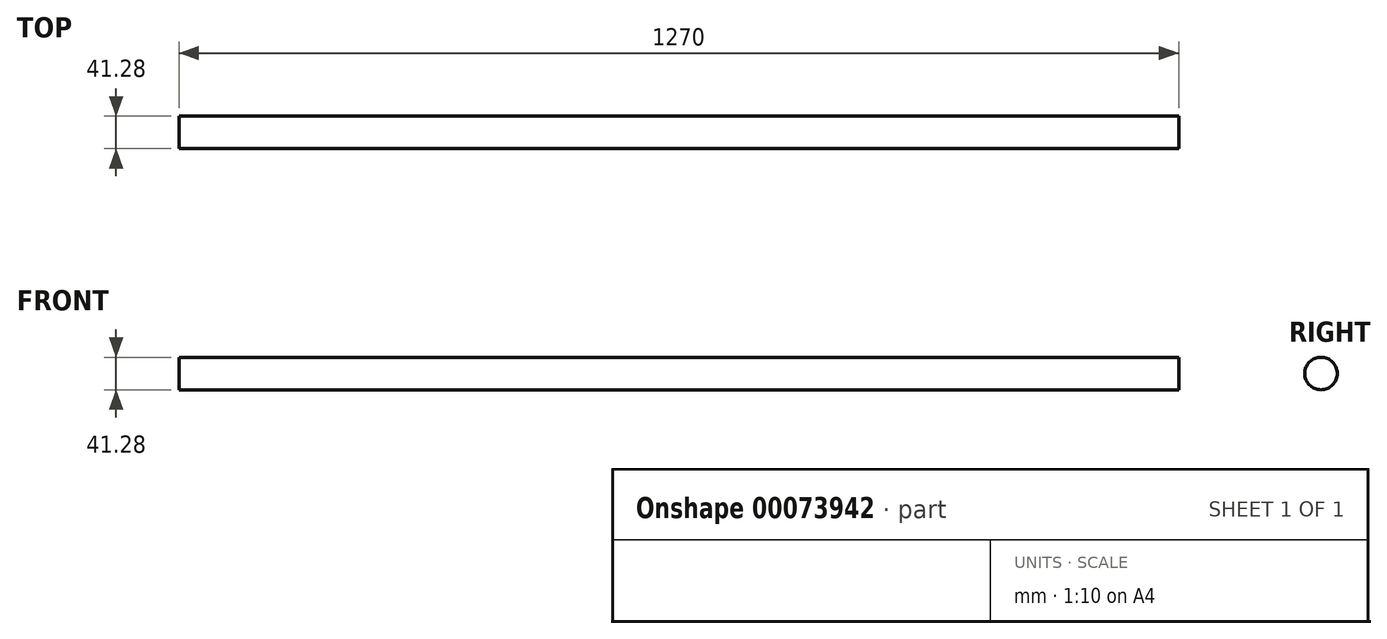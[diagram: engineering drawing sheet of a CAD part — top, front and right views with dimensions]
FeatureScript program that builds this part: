
annotation { "Feature Type Name" : "Feature", "Feature Type Description" : "" }
export const myFeature = defineFeature(function(context is Context, id is Id, definition is map)
    precondition{}
    {
        {
            var Q0;
            Q0=qCreatedBy(makeId("Front.planeOp"),FACE);
            var sketch = newSketch(context, id + "F0", { "sketchPlane" : qUnion([Q0])});
            skCircle(sketch, "E0", {"center": v(0, 0) * mm, "radius": 20.64 * mm});
            skSolve(sketch);
        }
        {
            var Q0;
            Q0=makeQuery(id+"F0.imprint","IMPRINT",FACE,{"disambiguationData":[TD([[makeQuery(id+"F0.imprint","IMPRINT",EDGE,{"derivedFrom":sQuery(id+"F0.wireOp",EDGE,"E0")}),1.0]])]});
            extrude(context, id + "F1", {"entities" : qUnion([Q0]), "depth" : 1219.2 * mm});
        }
        {
            var Q0;
            Q0=makeQuery(id+"F1.opExtrude","SWEPT_BODY",BODY,{"disambiguationData":[OSD([sQuery(id+"F0.wireOp",EDGE,"E0")])]});
            deleteBodies(context, id + "F2", {"entities" : qUnion([Q0])});
        }
        {
            var Q0;
            Q0=qCreatedBy(makeId("Right.planeOp"),FACE);
            var sketch = newSketch(context, id + "F3", { "sketchPlane" : qUnion([Q0])});
            skCircle(sketch, "E1", {"center": v(0, 0) * mm, "radius": 20.64 * mm});
            skSolve(sketch);
        }
        {
            var Q0;
            Q0=makeQuery(id+"F3.imprint","IMPRINT",FACE,{"disambiguationData":[TD([[makeQuery(id+"F3.imprint","IMPRINT",EDGE,{"derivedFrom":sQuery(id+"F3.wireOp",EDGE,"E1")}),1.0]])]});
            extrude(context, id + "F4", {"entities" : qUnion([Q0]), "depth" : 1270 * mm});
        }
    });
